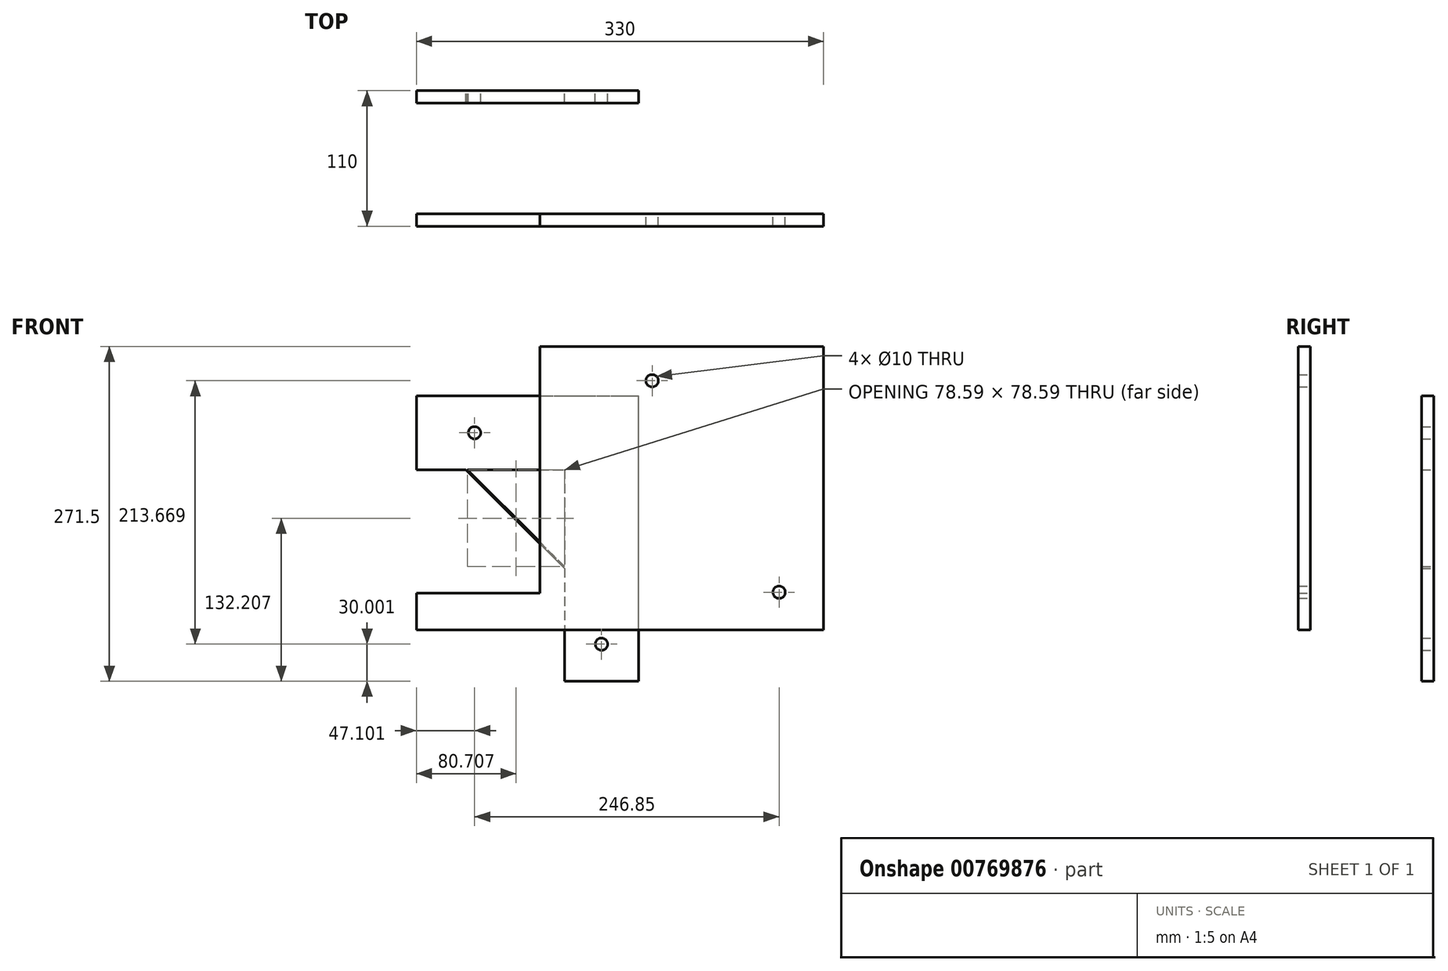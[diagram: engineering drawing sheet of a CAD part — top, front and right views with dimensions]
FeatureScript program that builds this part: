
annotation { "Feature Type Name" : "Feature", "Feature Type Description" : "" }
export const myFeature = defineFeature(function(context is Context, id is Id, definition is map)
    precondition{}
    {
        {
            var Q0;
            Q0=qCreatedBy(makeId("Front.planeOp"),FACE);
            var sketch = newSketch(context, id + "F0", { "sketchPlane" : qUnion([Q0])});
            skLineSegment(sketch, "E0.bottom", {"start": v(0, 300) * mm, "end": v(300, 300) * mm});
            skLineSegment(sketch, "E0.top", {"start": v(0, 200) * mm, "end": v(300, 200) * mm});
            skLineSegment(sketch, "E0.left", {"start": v(0, 300) * mm, "end": v(0, 200) * mm});
            skLineSegment(sketch, "E0.right", {"start": v(300, 300) * mm, "end": v(300, 200) * mm});
            skPoint(sketch, "E1", {"position": v(240, 300) * mm});
            skPoint(sketch, "E2", {"position": v(300, 240) * mm});
            skLineSegment(sketch, "E3", {"start": v(240, 300) * mm, "end": v(300, 240) * mm});
            skLineSegment(sketch, "E4", {"start": v(0, 235) * mm, "end": v(300, 235) * mm, "construction": true});
            skLineSegment(sketch, "E5", {"start": v(300, 214) * mm, "end": v(279, 235) * mm});
            skLineSegment(sketch, "E6", {"start": v(240, 300) * mm, "end": v(279, 235) * mm});
            skLineSegment(sketch, "E7", {"start": v(259.5, 267.5) * mm, "end": v(516.75, 421.85) * mm});
            skLineSegment(sketch, "E8", {"start": v(240, 300) * mm, "end": v(383.95, 342.17) * mm, "construction": true});
            skLineSegment(sketch, "E9", {"start": v(247.1, 330) * mm, "end": v(391.05, 372.17) * mm});
            skLineSegment(sketch, "E10", {"start": v(391.05, 372.17) * mm, "end": v(493.95, 200.67) * mm});
            skLineSegment(sketch, "E11", {"start": v(493.95, 200.67) * mm, "end": v(350, 158.5) * mm});
            skSolve(sketch);
        }
        {
            var Q0;
            Q0=qCreatedBy(makeId("Front.planeOp"),FACE);
            cPlane(context, id + "F1", {"entities" : qUnion([Q0]), "cplaneType" : CPlaneType.OFFSET, "offset" : 100 * mm, "width" : 150 * mm, "height" : 150 * mm});
        }
        {
            var Q0;
            Q0=qCreatedBy(id+"F1.planeOp",FACE);
            var sketch = newSketch(context, id + "F2", { "sketchPlane" : qUnion([Q0])});
            skLineSegment(sketch, "E12.0", {"start": v(0, 300) * mm, "end": v(240, 300) * mm, "construction": true});
            skLineSegment(sketch, "E13.0", {"start": v(300, 300) * mm, "end": v(300, 200) * mm, "construction": true});
            skLineSegment(sketch, "E14.0", {"start": v(247.1, 330) * mm, "end": v(391.05, 372.17) * mm, "construction": true});
            skLineSegment(sketch, "E15.0", {"start": v(391.05, 372.17) * mm, "end": v(493.95, 200.67) * mm, "construction": true});
            skLineSegment(sketch, "E16.0", {"start": v(493.95, 200.67) * mm, "end": v(350, 158.5) * mm, "construction": true});
            skLineSegment(sketch, "E17", {"start": v(200, 300) * mm, "end": v(200, 360) * mm});
            skLineSegment(sketch, "E18", {"start": v(200, 300) * mm, "end": v(320, 300) * mm});
            skLineSegment(sketch, "E19", {"start": v(320, 300) * mm, "end": v(320, 221.41) * mm});
            skLineSegment(sketch, "E20", {"start": v(320, 128.5) * mm, "end": v(380, 128.5) * mm});
            skLineSegment(sketch, "E21", {"start": v(380, 128.5) * mm, "end": v(380, 360) * mm});
            skLineSegment(sketch, "E22", {"start": v(200, 360) * mm, "end": v(380, 360) * mm});
            skCircle(sketch, "E23", {"center": v(247.1, 330) * mm, "radius": 5 * mm});
            skCircle(sketch, "E24", {"center": v(350, 158.5) * mm, "radius": 5 * mm});
            skLineSegment(sketch, "E25.0", {"start": v(240, 300) * mm, "end": v(300, 240) * mm, "construction": true});
            skLineSegment(sketch, "E26", {"start": v(240, 300) * mm, "end": v(320, 220) * mm});
            skLineSegment(sketch, "E27", {"start": v(247.1, 330) * mm, "end": v(200, 330) * mm, "construction": true});
            skLineSegment(sketch, "E28.trimOffspring", {"start": v(241.41, 300) * mm, "end": v(320, 221.41) * mm});
            skPoint(sketch, "E29.orphan", {"position": v(350, 190) * mm});
            skLineSegment(sketch, "E30.trimOffspring", {"start": v(350, 191.41) * mm, "end": v(350.7, 190.7) * mm});
            skLineSegment(sketch, "E31.trimOffspring", {"start": v(241.41, 300) * mm, "end": v(300, 300) * mm, "construction": true});
            skLineSegment(sketch, "E32.trimOffspring", {"start": v(320, 220) * mm, "end": v(320, 128.5) * mm});
            skSolve(sketch);
        }
        {
            var Q0;
            {var subQ1=sQuery(id+"F2.wireOp",EDGE,"E17");Q0=makeQuery(id+"F2.imprint","IMPRINT",FACE,{"disambiguationData":[TD([[makeQuery(id+"F2.imprint","IMPRINT",EDGE,{"derivedFrom":subQ1}),-1.0]])]});}
            extrude(context, id + "F3", {"entities" : qUnion([Q0]), "depth" : 10 * mm, "offsetDistance" : 25 * mm});
        }
        {
            var Q0;
            Q0=qCreatedBy(makeId("Front.planeOp"),FACE);
            cPlane(context, id + "F4", {"entities" : qUnion([Q0]), "cplaneType" : CPlaneType.OFFSET, "offset" : 200 * mm, "width" : 150 * mm, "height" : 150 * mm});
        }
        {
            var Q0;
            Q0=qCreatedBy(id+"F4.planeOp",FACE);
            var sketch = newSketch(context, id + "F5", { "sketchPlane" : qUnion([Q0])});
            skLineSegment(sketch, "E33", {"start": v(300, 200) * mm, "end": v(300, 400) * mm});
            skLineSegment(sketch, "E34", {"start": v(300, 400) * mm, "end": v(530, 400) * mm});
            skLineSegment(sketch, "E35", {"start": v(530, 400) * mm, "end": v(530, 170) * mm});
            skLineSegment(sketch, "E36", {"start": v(530, 170) * mm, "end": v(200, 170) * mm});
            skLineSegment(sketch, "E37", {"start": v(200, 170) * mm, "end": v(200, 200) * mm});
            skLineSegment(sketch, "E38", {"start": v(200, 200) * mm, "end": v(300, 200) * mm});
            skPoint(sketch, "E39.0", {"position": v(493.95, 200.67) * mm});
            skPoint(sketch, "E40.0", {"position": v(391.05, 372.17) * mm});
            skLineSegment(sketch, "E41.0", {"start": v(391.05, 372.17) * mm, "end": v(493.95, 200.67) * mm, "construction": true});
            skPoint(sketch, "E42.0", {"position": v(300, 200) * mm});
            skCircle(sketch, "E43", {"center": v(493.95, 200.67) * mm, "radius": 5 * mm});
            skCircle(sketch, "E44", {"center": v(391.05, 372.17) * mm, "radius": 5 * mm});
            skSolve(sketch);
        }
        {
            var Q0;
            Q0=makeQuery(id+"F5.imprint","IMPRINT",FACE,{"disambiguationData":[TD([[makeQuery(id+"F5.imprint","IMPRINT",EDGE,{"derivedFrom":sQuery(id+"F5.wireOp",EDGE,"E33")}),-1.0]])]});
            extrude(context, id + "F6", {"entities" : qUnion([Q0]), "depth" : 10 * mm, "offsetDistance" : 25 * mm});
        }
    });
